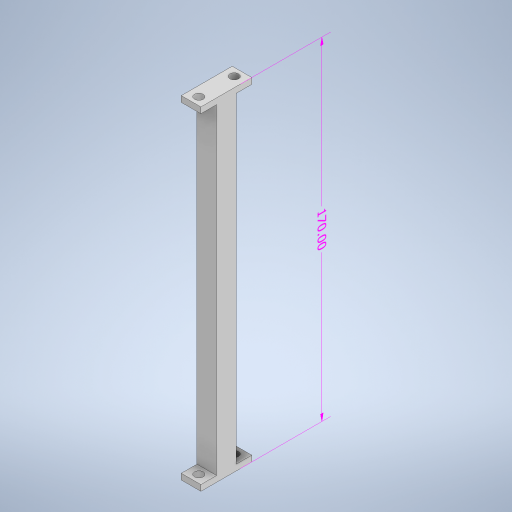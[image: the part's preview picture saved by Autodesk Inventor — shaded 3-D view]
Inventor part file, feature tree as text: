
AUTODESK INVENTOR PART (.ipt)
format: ipt  version: 2024 (Build 280153000, 153)  size: 279,552 bytes
history: native  units: mm
features: other x2, extrude x2, sketch x2, mirror x1
ambient origin geometry x8: Origin, YZ Plane, XZ Plane, XY Plane, X Axis, Y Axis, Z Axis, Center Point
bodies: Solid1 (feature_tree)
feature tree (7):
  other  "Annotations"
  extrude  "Extrusion1"  Depth=10.0mm
  extrude  "Extrusion2"  Depth=170.0mm
  mirror  "Mirror1"
  sketch  "Sketch1"  dims[d0=10.0mm d1=10.0mm]
  sketch  "Sketch2"  dims[d2=4.5mm d4=4.0mm d6=3.0mm d7=0.0mm d8=10.0mm d9=82.0mm d10=0.0mm d17=4.0mm d14=4.390242mm d15=3.280346mm d16=170.0mm]
  other  "Linear Dimension 1"
